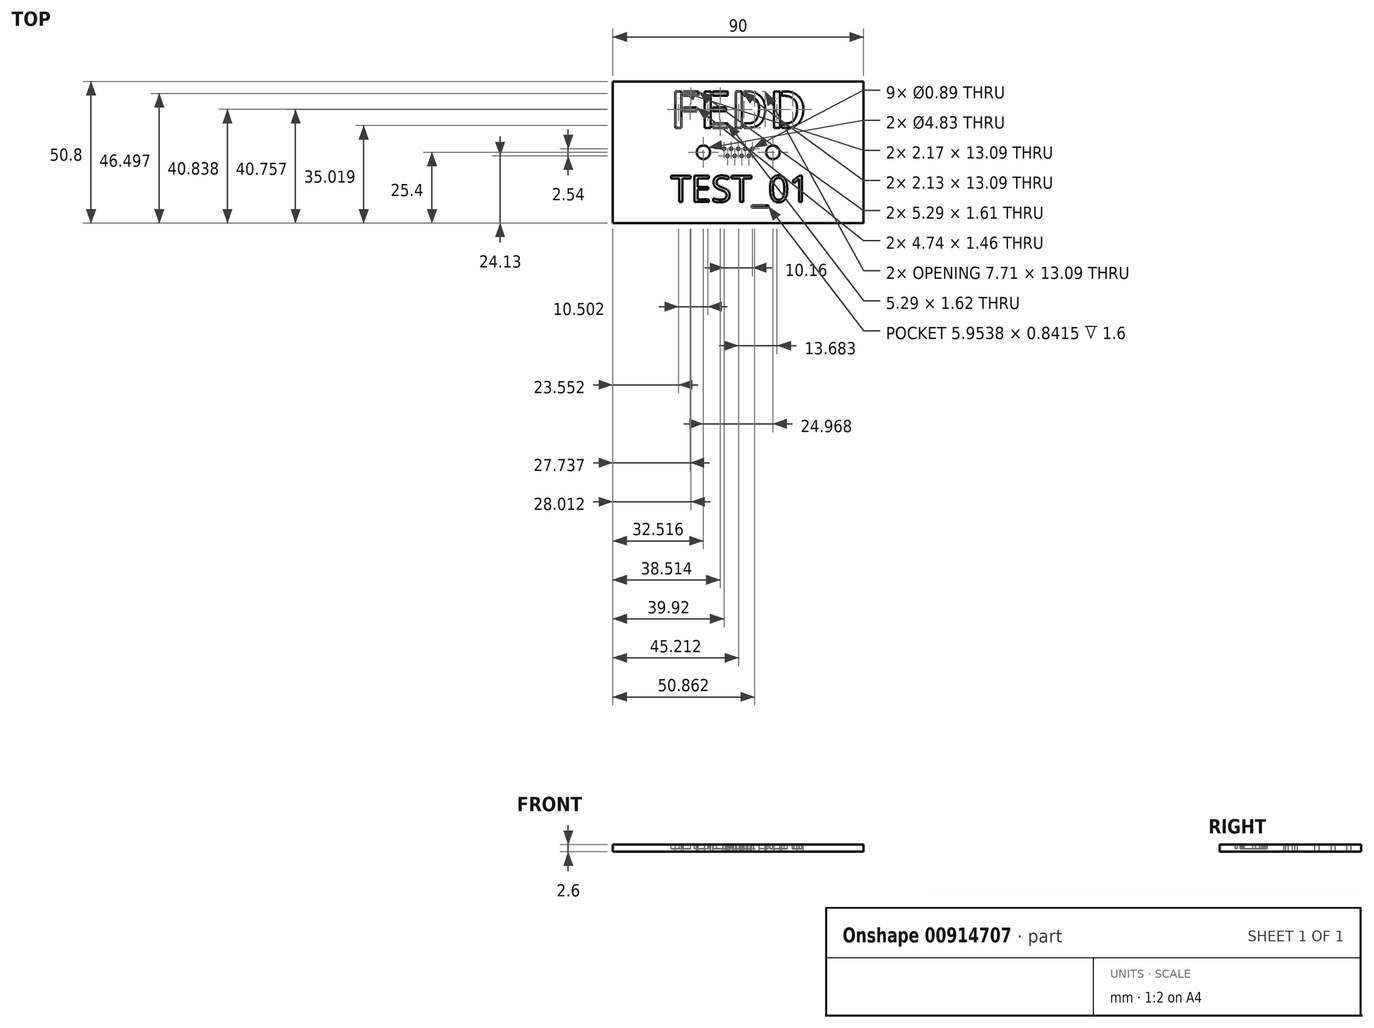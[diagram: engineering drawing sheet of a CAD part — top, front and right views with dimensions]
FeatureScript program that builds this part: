
annotation { "Feature Type Name" : "Feature", "Feature Type Description" : "" }
export const myFeature = defineFeature(function(context is Context, id is Id, definition is map)
    precondition{}
    {
        {
            var Q0;
            Q0=qCreatedBy(makeId("Front.planeOp"),FACE);
            var sketch = newSketch(context, id + "F0", { "sketchPlane" : qUnion([Q0])});
            skLineSegment(sketch, "E0.bottom", {"start": v(45, -1.3) * mm, "end": v(-45, -1.3) * mm});
            skLineSegment(sketch, "E0.top", {"start": v(45, 1.3) * mm, "end": v(-45, 1.3) * mm});
            skLineSegment(sketch, "E0.left", {"start": v(45, -1.3) * mm, "end": v(45, 1.3) * mm});
            skLineSegment(sketch, "E0.right", {"start": v(-45, -1.3) * mm, "end": v(-45, 1.3) * mm});
            skPoint(sketch, "E0.middle", {"position": v(0, 0) * mm});
            skSolve(sketch);
        }
        {
            var Q0;
            Q0=makeQuery(id+"F0.imprint","IMPRINT",FACE,{"disambiguationData":[TD([[makeQuery(id+"F0.imprint","IMPRINT",EDGE,{"derivedFrom":sQuery(id+"F0.wireOp",EDGE,"E0.bottom")}),-1.0]])]});
            extrude(context, id + "F1", {"entities" : qUnion([Q0]), "endBound" : BoundingType.SYMMETRIC, "depth" : 50.8 * mm, "offsetDistance" : 25.4 * mm});
        }
        {
            var Q0;
            Q0=makeQuery(id+"F1.opExtrude","SWEPT_FACE",FACE,{"disambiguationData":[OSD([sQuery(id+"F0.wireOp",EDGE,"E0.top")])]});
            var sketch = newSketch(context, id + "F2", { "sketchPlane" : qUnion([Q0])});
            skCircle(sketch, "E1", {"center": v(0, 1.27) * mm, "radius": 0.44 * mm});
            skSolve(sketch);
        }
        {
            var Q0;
            Q0=makeQuery(id+"F2.imprint","IMPRINT",FACE,{"disambiguationData":[TD([[makeQuery(id+"F2.imprint","IMPRINT",EDGE,{"derivedFrom":sQuery(id+"F2.wireOp",EDGE,"E1")}),1.0]])]});
            var Q1;
            Q1=sQuery(id+"F2.wireOp",EDGE,"E1");
            extrude(context, id + "F3", {"entities" : qUnion([Q0]), "operationType" : NewBodyOperationType.REMOVE, "surfaceOperationType" : NewSurfaceOperationType.ADD, "surfaceEntities" : qUnion([Q1]), "oppositeDirection" : true, "depth" : 2.6 * mm, "offsetDistance" : 25.4 * mm});
        }
        {
            var Q0;
            Q0=makeQuery(id+"F1.opExtrude","SWEPT_FACE",FACE,{"disambiguationData":[OSD([sQuery(id+"F0.wireOp",EDGE,"E0.bottom")])]});
            var sketch = newSketch(context, id + "F4", { "sketchPlane" : qUnion([Q0])});
            skCircle(sketch, "E2", {"center": v(2.54, -1.27) * mm, "radius": 0.44 * mm});
            skCircle(sketch, "E3", {"center": v(5.08, -1.27) * mm, "radius": 0.44 * mm});
            skCircle(sketch, "E4", {"center": v(-2.54, -1.27) * mm, "radius": 0.44 * mm});
            skCircle(sketch, "E5", {"center": v(-5.08, -1.27) * mm, "radius": 0.44 * mm});
            skCircle(sketch, "E6", {"center": v(1.27, 1.27) * mm, "radius": 0.44 * mm});
            skCircle(sketch, "E7", {"center": v(3.81, 1.27) * mm, "radius": 0.44 * mm});
            skCircle(sketch, "E8", {"center": v(-1.27, 1.27) * mm, "radius": 0.44 * mm});
            skCircle(sketch, "E9", {"center": v(-3.81, 1.27) * mm, "radius": 0.44 * mm});
            skCircle(sketch, "E10", {"center": v(12.48, 0) * mm, "radius": 2.41 * mm});
            skCircle(sketch, "E11", {"center": v(-12.48, 0) * mm, "radius": 2.41 * mm});
            skSolve(sketch);
        }
        {
            var Q0;
            Q0=makeQuery(id+"F4.imprint","IMPRINT",FACE,{"disambiguationData":[TD([[makeQuery(id+"F4.imprint","IMPRINT",EDGE,{"derivedFrom":sQuery(id+"F4.wireOp",EDGE,"E10")}),1.0]])]});
            var Q1;
            Q1=sQuery(id+"F4.wireOp",EDGE,"E10");
            extrude(context, id + "F5", {"entities" : qUnion([Q0]), "operationType" : NewBodyOperationType.REMOVE, "surfaceEntities" : qUnion([Q1]), "oppositeDirection" : true, "depth" : 2.3 * mm, "offsetDistance" : 25.4 * mm});
        }
        {
            var Q0;
            Q0=makeQuery(id+"F4.imprint","IMPRINT",FACE,{"disambiguationData":[TD([[makeQuery(id+"F4.imprint","IMPRINT",EDGE,{"derivedFrom":sQuery(id+"F4.wireOp",EDGE,"E3")}),1.0]])]});
            var Q1;
            Q1=makeQuery(id+"F4.imprint","IMPRINT",FACE,{"disambiguationData":[TD([[makeQuery(id+"F4.imprint","IMPRINT",EDGE,{"derivedFrom":sQuery(id+"F4.wireOp",EDGE,"E7")}),1.0]])]});
            var Q2;
            Q2=makeQuery(id+"F4.imprint","IMPRINT",FACE,{"disambiguationData":[TD([[makeQuery(id+"F4.imprint","IMPRINT",EDGE,{"derivedFrom":sQuery(id+"F4.wireOp",EDGE,"E6")}),1.0]])]});
            var Q3;
            Q3=makeQuery(id+"F4.imprint","IMPRINT",FACE,{"disambiguationData":[TD([[makeQuery(id+"F4.imprint","IMPRINT",EDGE,{"derivedFrom":sQuery(id+"F4.wireOp",EDGE,"E2")}),1.0]])]});
            var Q4;
            Q4=makeQuery(id+"F4.imprint","IMPRINT",FACE,{"disambiguationData":[TD([[makeQuery(id+"F4.imprint","IMPRINT",EDGE,{"derivedFrom":sQuery(id+"F4.wireOp",EDGE,"E4")}),1.0]])]});
            var Q5;
            Q5=makeQuery(id+"F4.imprint","IMPRINT",FACE,{"disambiguationData":[TD([[makeQuery(id+"F4.imprint","IMPRINT",EDGE,{"derivedFrom":sQuery(id+"F4.wireOp",EDGE,"E8")}),1.0]])]});
            var Q6;
            Q6=makeQuery(id+"F4.imprint","IMPRINT",FACE,{"disambiguationData":[TD([[makeQuery(id+"F4.imprint","IMPRINT",EDGE,{"derivedFrom":sQuery(id+"F4.wireOp",EDGE,"E9")}),1.0]])]});
            var Q7;
            Q7=makeQuery(id+"F4.imprint","IMPRINT",FACE,{"disambiguationData":[TD([[makeQuery(id+"F4.imprint","IMPRINT",EDGE,{"derivedFrom":sQuery(id+"F4.wireOp",EDGE,"E5")}),1.0]])]});
            var Q8;
            Q8=makeQuery(id+"F4.imprint","IMPRINT",FACE,{"disambiguationData":[TD([[makeQuery(id+"F4.imprint","IMPRINT",EDGE,{"derivedFrom":sQuery(id+"F4.wireOp",EDGE,"E11")}),1.0]])]});
            extrude(context, id + "F6", {"entities" : qUnion([Q0, Q1, Q2, Q3, Q4, Q5, Q6, Q7, Q8]), "operationType" : NewBodyOperationType.REMOVE, "oppositeDirection" : true, "depth" : 2.6 * mm, "offsetDistance" : 25.4 * mm});
        }
        {
            var Q0;
            Q0=makeQuery(id+"F4.imprint","IMPRINT",FACE,{"disambiguationData":[TD([[makeQuery(id+"F4.imprint","IMPRINT",EDGE,{"derivedFrom":sQuery(id+"F4.wireOp",EDGE,"E10")}),1.0]])]});
            var Q1;
            Q1=sQuery(id+"F4.wireOp",EDGE,"E10");
            extrude(context, id + "F7", {"entities" : qUnion([Q0]), "operationType" : NewBodyOperationType.REMOVE, "surfaceEntities" : qUnion([Q1]), "oppositeDirection" : true, "depth" : 2.6 * mm, "offsetDistance" : 25.4 * mm});
        }
        {
            var Q0;
            Q0=makeQuery(id+"F1.opExtrude","SWEPT_FACE",FACE,{"disambiguationData":[OSD([sQuery(id+"F0.wireOp",EDGE,"E0.top")])]});
            var sketch = newSketch(context, id + "F8", { "sketchPlane" : qUnion([Q0])});
            skText(sketch, "E12", { "text": "FEDD", "fontName": "AllertaStencil-Regular.ttf"});
            const initialGuessF8  = {"E12": [-0.02422, 0.00881, 1, 0, 0.0131]};
            skSetInitialGuess(sketch, initialGuessF8);
            skSolve(sketch);
        }
        {
            var Q0;
            Q0=makeQuery(id+"F8.imprint","IMPRINT",FACE,{"disambiguationData":[TD([[makeQuery(id+"F8.imprint","IMPRINT",EDGE,{"derivedFrom":sQuery(id+"F8.wireOp",EDGE,"E12.sketch_text.stroke-0")}),1.0]])]});
            var sketch = newSketch(context, id + "F9", { "sketchPlane" : qUnion([Q0])});
            skText(sketch, "E13", { "text": "TEST_01", "fontName": "OpenSans-Regular.ttf"});
            const initialGuessF9  = {"E13": [-0.02427, -0.01782, 1, 0, 0.00948]};
            skSetInitialGuess(sketch, initialGuessF9);
            skSolve(sketch);
        }
        {
            var Q0;
            Q0=makeQuery(id+"F8.imprint","IMPRINT",FACE,{"disambiguationData":[TD([[makeQuery(id+"F8.imprint","IMPRINT",EDGE,{"derivedFrom":sQuery(id+"F8.wireOp",EDGE,"E12.sketch_text.stroke-0")}),-1.0]])]});
            var Q1;
            Q1=makeQuery(id+"F8.imprint","IMPRINT",FACE,{"disambiguationData":[TD([[makeQuery(id+"F8.imprint","IMPRINT",EDGE,{"derivedFrom":sQuery(id+"F8.wireOp",EDGE,"E12.sketch_text.stroke-4")}),-1.0]])]});
            var Q2;
            Q2=makeQuery(id+"F8.imprint","IMPRINT",FACE,{"disambiguationData":[TD([[makeQuery(id+"F8.imprint","IMPRINT",EDGE,{"derivedFrom":sQuery(id+"F8.wireOp",EDGE,"E12.sketch_text.stroke-8")}),-1.0]])]});
            var Q3;
            Q3=makeQuery(id+"F8.imprint","IMPRINT",FACE,{"disambiguationData":[TD([[makeQuery(id+"F8.imprint","IMPRINT",EDGE,{"derivedFrom":sQuery(id+"F8.wireOp",EDGE,"E12.sketch_text.stroke-12")}),-1.0]])]});
            var Q4;
            Q4=makeQuery(id+"F8.imprint","IMPRINT",FACE,{"disambiguationData":[TD([[makeQuery(id+"F8.imprint","IMPRINT",EDGE,{"derivedFrom":sQuery(id+"F8.wireOp",EDGE,"E12.sketch_text.stroke-16")}),-1.0]])]});
            var Q5;
            Q5=makeQuery(id+"F8.imprint","IMPRINT",FACE,{"disambiguationData":[TD([[makeQuery(id+"F8.imprint","IMPRINT",EDGE,{"derivedFrom":sQuery(id+"F8.wireOp",EDGE,"E12.sketch_text.stroke-20")}),-1.0]])]});
            var Q6;
            Q6=makeQuery(id+"F8.imprint","IMPRINT",FACE,{"disambiguationData":[TD([[makeQuery(id+"F8.imprint","IMPRINT",EDGE,{"derivedFrom":sQuery(id+"F8.wireOp",EDGE,"E12.sketch_text.stroke-28")}),-1.0]])]});
            var Q7;
            Q7=makeQuery(id+"F9.imprint","IMPRINT",FACE,{"disambiguationData":[TD([[makeQuery(id+"F9.imprint","IMPRINT",EDGE,{"derivedFrom":makeQuery(id+"F8.imprint","IMPRINT",EDGE,{"derivedFrom":sQuery(id+"F8.wireOp",EDGE,"E12.sketch_text.stroke-32")})}),-1.0]])]});
            var Q8;
            Q8=makeQuery(id+"F8.imprint","IMPRINT",FACE,{"disambiguationData":[TD([[makeQuery(id+"F8.imprint","IMPRINT",EDGE,{"derivedFrom":sQuery(id+"F8.wireOp",EDGE,"E12.sketch_text.stroke-24")}),-1.0]])]});
            var Q9;
            Q9=makeQuery(id+"F8.imprint","IMPRINT",FACE,{"disambiguationData":[TD([[makeQuery(id+"F8.imprint","IMPRINT",EDGE,{"derivedFrom":sQuery(id+"F8.wireOp",EDGE,"E12.sketch_text.stroke-54")}),-1.0]])]});
            var Q10;
            Q10=makeQuery(id+"F9.imprint","IMPRINT",FACE,{"disambiguationData":[TD([[makeQuery(id+"F9.imprint","IMPRINT",EDGE,{"derivedFrom":makeQuery(id+"F8.imprint","IMPRINT",EDGE,{"derivedFrom":sQuery(id+"F8.wireOp",EDGE,"E12.sketch_text.stroke-58")})}),-1.0]])]});
            extrude(context, id + "F10", {"entities" : qUnion([Q0, Q1, Q2, Q3, Q4, Q5, Q6, Q7, Q8, Q9, Q10]), "operationType" : NewBodyOperationType.REMOVE, "oppositeDirection" : true, "depth" : 2.6 * mm, "offsetDistance" : 25.4 * mm});
        }
        {
            var Q0;
            Q0=makeQuery(id+"F9.imprint","IMPRINT",FACE,{"disambiguationData":[TD([[makeQuery(id+"F9.imprint","IMPRINT",EDGE,{"derivedFrom":sQuery(id+"F9.wireOp",EDGE,"E13.sketch_text.stroke-0")}),-1.0]])]});
            var Q1;
            Q1=makeQuery(id+"F9.imprint","IMPRINT",FACE,{"disambiguationData":[TD([[makeQuery(id+"F9.imprint","IMPRINT",EDGE,{"derivedFrom":sQuery(id+"F9.wireOp",EDGE,"E13.sketch_text.stroke-8")}),-1.0]])]});
            var Q2;
            Q2=makeQuery(id+"F9.imprint","IMPRINT",FACE,{"disambiguationData":[TD([[makeQuery(id+"F9.imprint","IMPRINT",EDGE,{"derivedFrom":sQuery(id+"F9.wireOp",EDGE,"E13.sketch_text.stroke-20")}),-1.0]])]});
            var Q3;
            Q3=makeQuery(id+"F9.imprint","IMPRINT",FACE,{"disambiguationData":[TD([[makeQuery(id+"F9.imprint","IMPRINT",EDGE,{"derivedFrom":sQuery(id+"F9.wireOp",EDGE,"E13.sketch_text.stroke-45")}),-1.0]])]});
            var Q4;
            Q4=makeQuery(id+"F9.imprint","IMPRINT",FACE,{"disambiguationData":[TD([[makeQuery(id+"F9.imprint","IMPRINT",EDGE,{"derivedFrom":sQuery(id+"F9.wireOp",EDGE,"E13.sketch_text.stroke-53")}),-1.0]])]});
            var Q5;
            Q5=makeQuery(id+"F9.imprint","IMPRINT",FACE,{"disambiguationData":[TD([[makeQuery(id+"F9.imprint","IMPRINT",EDGE,{"derivedFrom":sQuery(id+"F9.wireOp",EDGE,"E13.sketch_text.stroke-57")}),-1.0]])]});
            var Q6;
            Q6=makeQuery(id+"F9.imprint","IMPRINT",FACE,{"disambiguationData":[TD([[makeQuery(id+"F9.imprint","IMPRINT",EDGE,{"derivedFrom":sQuery(id+"F9.wireOp",EDGE,"E13.sketch_text.stroke-73")}),-1.0]])]});
            extrude(context, id + "F11", {"entities" : qUnion([Q0, Q1, Q2, Q3, Q4, Q5, Q6]), "operationType" : NewBodyOperationType.REMOVE, "oppositeDirection" : true, "depth" : 1.6 * mm, "offsetDistance" : 25.4 * mm});
        }
    });
